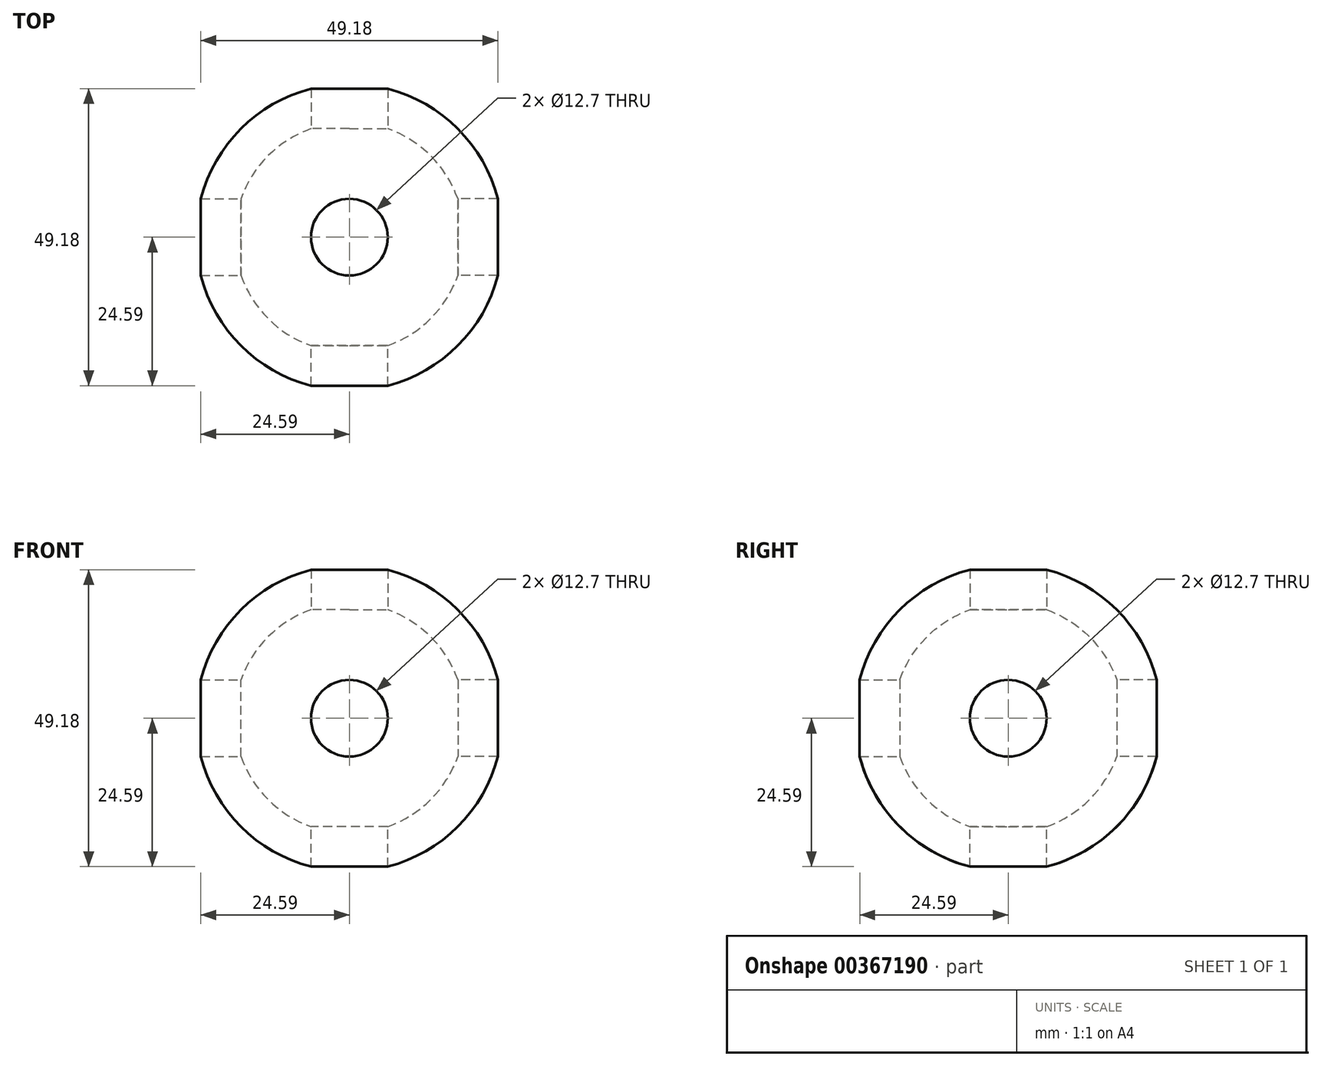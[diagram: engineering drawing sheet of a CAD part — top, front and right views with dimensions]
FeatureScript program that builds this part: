
annotation { "Feature Type Name" : "Feature", "Feature Type Description" : "" }
export const myFeature = defineFeature(function(context is Context, id is Id, definition is map)
    precondition{}
    {
        {
            var Q0;
            Q0=qCreatedBy(makeId("Top.planeOp"),FACE);
            var sketch = newSketch(context, id + "F0", { "sketchPlane" : qUnion([Q0])});
            skArc(sketch, "E0", {"start": v(0, -25.4) * mm, "mid": v(25.4, 0) * mm, "end": v(0, 25.4) * mm});
            skLineSegment(sketch, "E1", {"start": v(0, 25.4) * mm, "end": v(0, 19.05) * mm});
            skLineSegment(sketch, "E2", {"start": v(0, -19.05) * mm, "end": v(0, -25.4) * mm});
            skPoint(sketch, "E3.start.orphan", {"position": v(0, 19.05) * mm});
            skArc(sketch, "E4", {"start": v(0, -19.05) * mm, "mid": v(19.05, 0) * mm, "end": v(0, 19.05) * mm});
            skSolve(sketch);
        }
        {
            var Q0;
            Q0=makeQuery(id+"F0.imprint","IMPRINT",FACE,{"disambiguationData":[TD([[makeQuery(id+"F0.imprint","IMPRINT",EDGE,{"derivedFrom":sQuery(id+"F0.wireOp",EDGE,"E0")}),1.0]])]});
            var Q1;
            Q1=sQuery(id+"F0.wireOp",EDGE,"E1");
            revolve(context, id + "F1", {"entities" : qUnion([Q0]), "axis" : qUnion([Q1]), "revolveType" : RevolveType.FULL});
        }
        {
            var Q0;
            Q0=qCreatedBy(makeId("Top.planeOp"),FACE);
            var sketch = newSketch(context, id + "F2", { "sketchPlane" : qUnion([Q0])});
            skCircle(sketch, "E5", {"center": v(0, 0) * mm, "radius": 6.35 * mm});
            skSolve(sketch);
        }
        {
            var Q0;
            Q0 = qSketchRegion(id + "F2", true);
            extrude(context, id + "F3", {"entities" : qUnion([Q0]), "operationType" : NewBodyOperationType.REMOVE, "oppositeDirection" : true, "depth" : 59.18 * mm});
        }
        {
            var Q0;
            Q0=qCreatedBy(makeId("Right.planeOp"),FACE);
            var sketch = newSketch(context, id + "F4", { "sketchPlane" : qUnion([Q0])});
            skCircle(sketch, "E6", {"center": v(0, 0) * mm, "radius": 6.35 * mm});
            skSolve(sketch);
        }
        {
            var Q0;
            Q0 = qSketchRegion(id + "F4", true);
            extrude(context, id + "F5", {"entities" : qUnion([Q0]), "operationType" : NewBodyOperationType.REMOVE, "oppositeDirection" : true, "depth" : 25.4 * mm});
        }
        {
            var Q0;
            Q0=qCreatedBy(makeId("Front.planeOp"),FACE);
            var sketch = newSketch(context, id + "F6", { "sketchPlane" : qUnion([Q0])});
            skCircle(sketch, "E7", {"center": v(0, 0) * mm, "radius": 6.35 * mm});
            skSolve(sketch);
        }
        {
            var Q0;
            Q0 = qSketchRegion(id + "F6", true);
            extrude(context, id + "F7", {"entities" : qUnion([Q0]), "operationType" : NewBodyOperationType.REMOVE, "oppositeDirection" : true, "depth" : 25.4 * mm});
        }
        {
            var Q0;
            Q0=qCreatedBy(makeId("Right.planeOp"),FACE);
            var sketch = newSketch(context, id + "F8", { "sketchPlane" : qUnion([Q0])});
            skCircle(sketch, "E8", {"center": v(0, 0) * mm, "radius": 6.35 * mm});
            skSolve(sketch);
        }
        {
            var Q0;
            Q0 = qSketchRegion(id + "F8", true);
            extrude(context, id + "F9", {"entities" : qUnion([Q0]), "operationType" : NewBodyOperationType.REMOVE, "depth" : 39.12 * mm});
        }
        {
            var Q0;
            Q0=qCreatedBy(makeId("Front.planeOp"),FACE);
            var sketch = newSketch(context, id + "F10", { "sketchPlane" : qUnion([Q0])});
            skCircle(sketch, "E9", {"center": v(0, 0) * mm, "radius": 6.35 * mm});
            skSolve(sketch);
        }
        {
            var Q0;
            Q0 = qSketchRegion(id + "F10", true);
            extrude(context, id + "F11", {"entities" : qUnion([Q0]), "operationType" : NewBodyOperationType.REMOVE, "depth" : 44.45 * mm});
        }
        {
            var Q0;
            Q0=qCreatedBy(makeId("Top.planeOp"),FACE);
            var sketch = newSketch(context, id + "F12", { "sketchPlane" : qUnion([Q0])});
            skCircle(sketch, "E10", {"center": v(0, 0) * mm, "radius": 6.35 * mm});
            skSolve(sketch);
        }
        {
            var Q0;
            Q0 = qSketchRegion(id + "F12", true);
            extrude(context, id + "F13", {"entities" : qUnion([Q0]), "operationType" : NewBodyOperationType.REMOVE, "depth" : 41.15 * mm});
        }
    });
